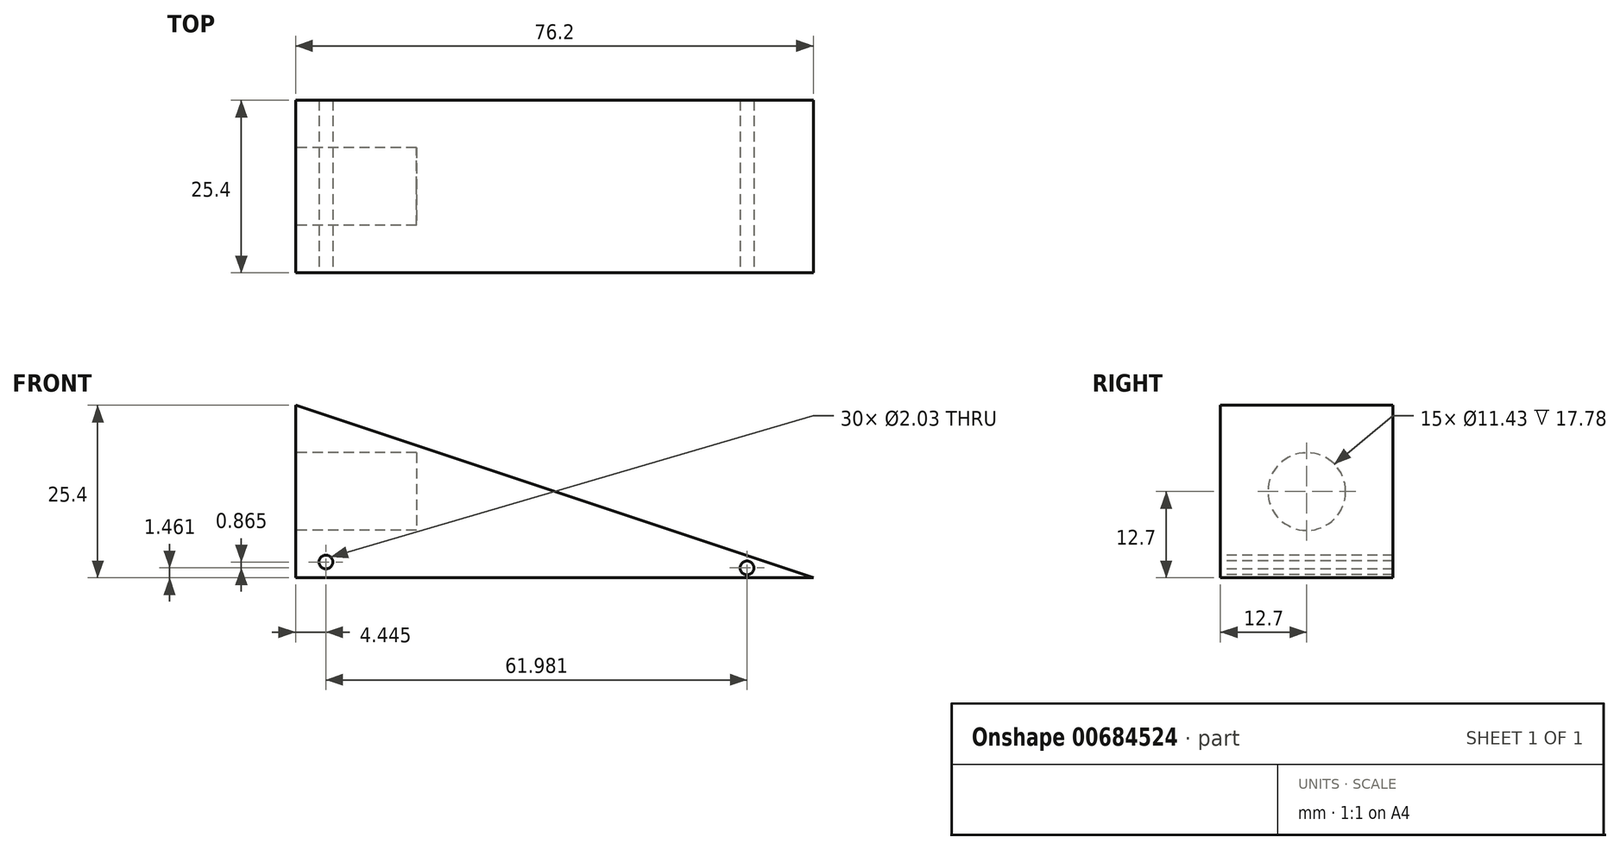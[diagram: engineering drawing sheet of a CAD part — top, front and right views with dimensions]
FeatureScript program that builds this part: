
annotation { "Feature Type Name" : "Feature", "Feature Type Description" : "" }
export const myFeature = defineFeature(function(context is Context, id is Id, definition is map)
    precondition{}
    {
        {
            var Q0;
            Q0=qCreatedBy(makeId("Front.planeOp"),FACE);
            var sketch = newSketch(context, id + "F0", { "sketchPlane" : qUnion([Q0])});
            skLineSegment(sketch, "E0", {"start": v(0, 0) * mm, "end": v(-76.2, 0) * mm});
            skLineSegment(sketch, "E1", {"start": v(-76.2, 0) * mm, "end": v(-76.2, 25.4) * mm});
            skLineSegment(sketch, "E2", {"start": v(-76.2, 25.4) * mm, "end": v(0, 0) * mm});
            skSolve(sketch);
        }
        {
            var Q0;
            Q0=makeQuery(id+"F0.imprint","IMPRINT",FACE,{"disambiguationData":[TD([[makeQuery(id+"F0.imprint","IMPRINT",EDGE,{"derivedFrom":sQuery(id+"F0.wireOp",EDGE,"E0")}),-1.0]])]});
            extrude(context, id + "F1", {"entities" : qUnion([Q0]), "depth" : 25.4 * mm, "offsetDistance" : 25.4 * mm});
        }
        {
            var Q0;
            Q0=makeQuery(id+"F1.opExtrude","SWEPT_FACE",FACE,{"disambiguationData":[OSD([sQuery(id+"F0.wireOp",EDGE,"E1")])]});
            var sketch = newSketch(context, id + "F2", { "sketchPlane" : qUnion([Q0])});
            skCircle(sketch, "E3", {"center": v(12.7, 12.7) * mm, "radius": 5.72 * mm});
            skPoint(sketch, "E3.centerSnap0", {"position": v(0, 12.7) * mm});
            skPoint(sketch, "E3.centerSnap1", {"position": v(12.7, 0) * mm});
            skSolve(sketch);
        }
        {
            var Q0;
            Q0=makeQuery(id+"F2.imprint","IMPRINT",FACE,{"disambiguationData":[TD([[makeQuery(id+"F2.imprint","IMPRINT",EDGE,{"derivedFrom":sQuery(id+"F2.wireOp",EDGE,"E3")}),1.0]])]});
            extrude(context, id + "F3", {"entities" : qUnion([Q0]), "operationType" : NewBodyOperationType.REMOVE, "oppositeDirection" : true, "depth" : 17.78 * mm, "offsetDistance" : 25.4 * mm});
        }
        {
            var Q0;
            Q0=makeQuery(id+"F1.opExtrude","CAP_FACE",FACE,{"disambiguationData":[OSD([sQuery(id+"F0.wireOp",EDGE,"E0"),sQuery(id+"F0.wireOp",EDGE,"E1"),sQuery(id+"F0.wireOp",EDGE,"E2")])],"isStart":false});
            var sketch = newSketch(context, id + "F4", { "sketchPlane" : qUnion([Q0])});
            skCircle(sketch, "E4", {"center": v(-71.76, 2.33) * mm, "radius": 1.02 * mm});
            skCircle(sketch, "E5", {"center": v(-11.01, 1.46) * mm, "radius": 1.02 * mm});
            skSolve(sketch);
        }
        {
            var Q0;
            Q0=makeQuery(id+"F4.imprint","IMPRINT",FACE,{"disambiguationData":[TD([[makeQuery(id+"F4.imprint","IMPRINT",EDGE,{"derivedFrom":sQuery(id+"F4.wireOp",EDGE,"E4")}),1.0]])]});
            extrude(context, id + "F5", {"entities" : qUnion([Q0]), "operationType" : NewBodyOperationType.REMOVE, "oppositeDirection" : true, "depth" : 25.4 * mm, "offsetDistance" : 25.4 * mm});
        }
        {
            var Q0;
            Q0=makeQuery(id+"F1.opExtrude","CAP_FACE",FACE,{"disambiguationData":[OSD([sQuery(id+"F0.wireOp",EDGE,"E0"),sQuery(id+"F0.wireOp",EDGE,"E1"),sQuery(id+"F0.wireOp",EDGE,"E2")])],"isStart":false});
            var sketch = newSketch(context, id + "F6", { "sketchPlane" : qUnion([Q0])});
            skCircle(sketch, "E6", {"center": v(-9.77, 1.46) * mm, "radius": 1.02 * mm});
            skSolve(sketch);
        }
        {
            var Q0;
            Q0=makeQuery(id+"F6.imprint","IMPRINT",FACE,{"disambiguationData":[TD([[makeQuery(id+"F6.imprint","IMPRINT",EDGE,{"derivedFrom":sQuery(id+"F6.wireOp",EDGE,"E6")}),1.0]])]});
            extrude(context, id + "F7", {"entities" : qUnion([Q0]), "operationType" : NewBodyOperationType.REMOVE, "oppositeDirection" : true, "depth" : 25.4 * mm, "offsetDistance" : 25.4 * mm});
        }
    });
